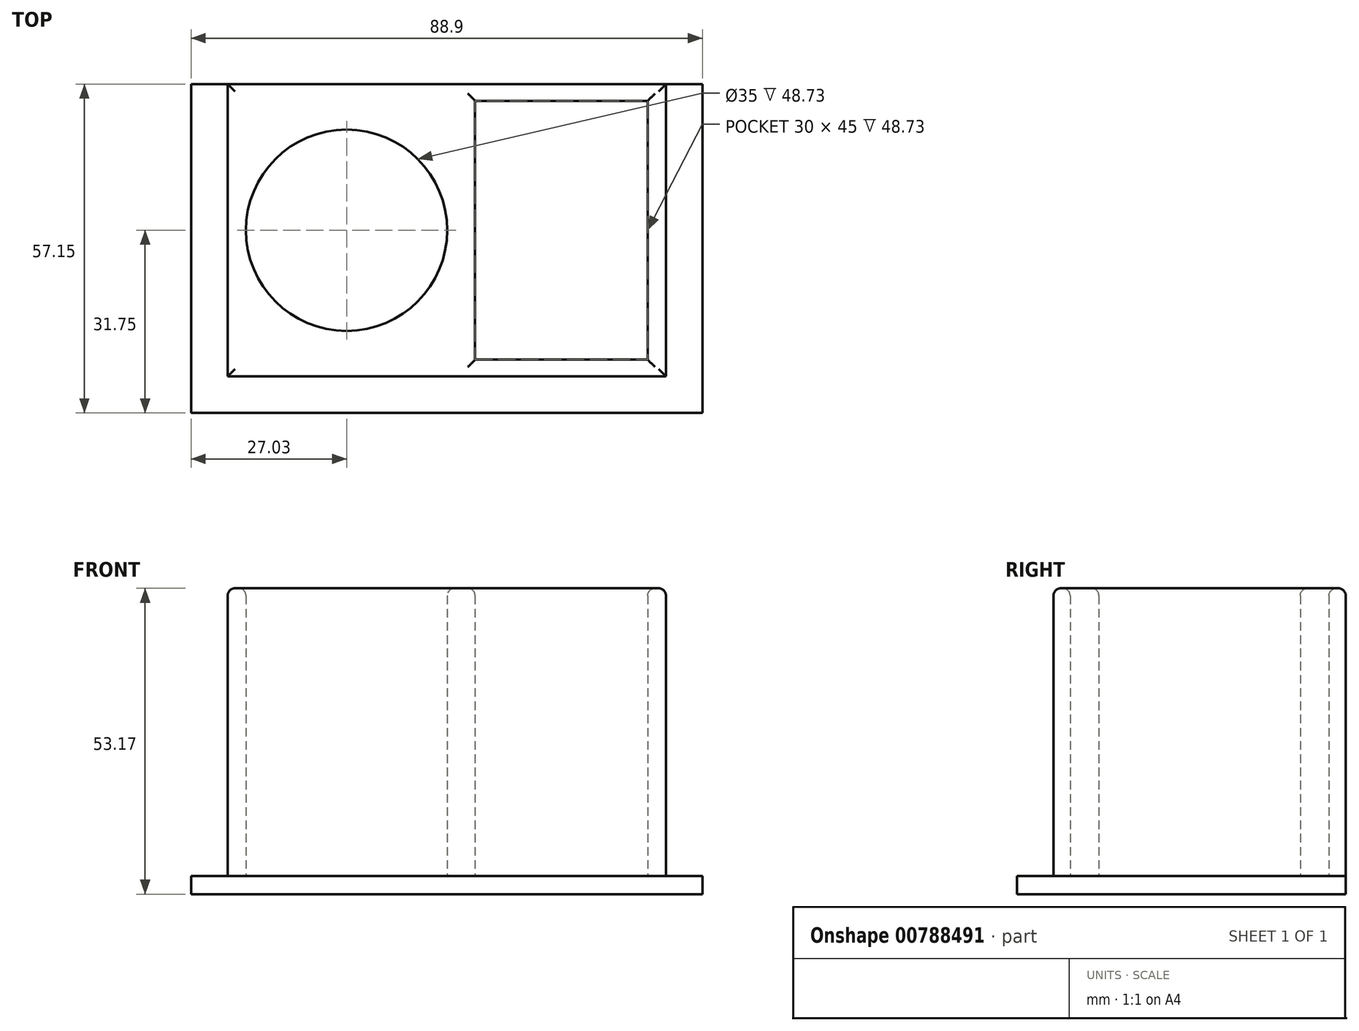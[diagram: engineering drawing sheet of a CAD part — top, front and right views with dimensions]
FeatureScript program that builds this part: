
annotation { "Feature Type Name" : "Feature", "Feature Type Description" : "" }
export const myFeature = defineFeature(function(context is Context, id is Id, definition is map)
    precondition{}
    {
        {
            var Q0;
            Q0=qCreatedBy(makeId("Top.planeOp"),FACE);
            var sketch = newSketch(context, id + "F0", { "sketchPlane" : qUnion([Q0])});
            skLineSegment(sketch, "E0.bottom", {"start": v(0, 0) * mm, "end": v(30, 0) * mm});
            skLineSegment(sketch, "E0.top", {"start": v(0, 45) * mm, "end": v(30, 45) * mm});
            skLineSegment(sketch, "E0.left", {"start": v(0, 0) * mm, "end": v(0, 45) * mm});
            skLineSegment(sketch, "E0.right", {"start": v(30, 0) * mm, "end": v(30, 45) * mm});
            skCircle(sketch, "E1", {"center": v(-22.35, 22.5) * mm, "radius": 17.5 * mm});
            skLineSegment(sketch, "E2.bottom", {"start": v(-43.03, 47.9) * mm, "end": v(33.17, 47.9) * mm});
            skLineSegment(sketch, "E2.top", {"start": v(-43.03, -2.9) * mm, "end": v(33.18, -2.9) * mm});
            skLineSegment(sketch, "E2.left", {"start": v(-43.03, 47.9) * mm, "end": v(-43.03, -2.9) * mm});
            skLineSegment(sketch, "E2.right", {"start": v(33.17, 47.9) * mm, "end": v(33.17, -2.9) * mm});
            skLineSegment(sketch, "E3", {"start": v(30, 22.5) * mm, "end": v(33.17, 22.5) * mm});
            skLineSegment(sketch, "E4", {"start": v(-43.03, 22.5) * mm, "end": v(-22.35, 22.5) * mm});
            skLineSegment(sketch, "E5", {"start": v(-43.03, 22.5) * mm, "end": v(-39.85, 22.5) * mm});
            skSolve(sketch);
        }
        {
            var Q0;
            {var subQ7=sQuery(id+"F0.wireOp",EDGE,"E0.bottom");Q0=makeQuery(id+"F0.imprint","IMPRINT",FACE,{"disambiguationData":[TD([[makeQuery(id+"F0.imprint","IMPRINT",EDGE,{"derivedFrom":subQ7}),-1.0]])]});}
            extrude(context, id + "F1", {"entities" : qUnion([Q0]), "depth" : 50 * mm, "offsetDistance" : 25.4 * mm});
        }
        {
            var Q0;
            Q0=makeQuery(id+"F1.opExtrude","CAP_FACE",FACE,{"disambiguationData":[OSD([sQuery(id+"F0.wireOp",EDGE,"E0.bottom"),sQuery(id+"F0.wireOp",EDGE,"E0.top"),sQuery(id+"F0.wireOp",EDGE,"E0.left"),sQuery(id+"F0.wireOp",EDGE,"E0.right"),sQuery(id+"F0.wireOp",EDGE,"E1"),sQuery(id+"F0.wireOp",EDGE,"E2.bottom"),sQuery(id+"F0.wireOp",EDGE,"E2.top"),sQuery(id+"F0.wireOp",EDGE,"E2.left"),sQuery(id+"F0.wireOp",EDGE,"E2.right")])],"isStart":true});
            var sketch = newSketch(context, id + "F2", { "sketchPlane" : qUnion([Q0])});
            skLineSegment(sketch, "E6.0", {"start": v(39.52, -54.25) * mm, "end": v(39.52, 9.25) * mm});
            skLineSegment(sketch, "E6.1", {"start": v(-49.38, -54.25) * mm, "end": v(39.52, -54.25) * mm});
            skLineSegment(sketch, "E6.2", {"start": v(-49.38, 9.25) * mm, "end": v(-49.38, -54.25) * mm});
            skLineSegment(sketch, "E6.3", {"start": v(39.52, 9.25) * mm, "end": v(-49.38, 9.25) * mm});
            skSolve(sketch);
        }
        {
            var Q0;
            Q0=makeQuery(id+"F2.imprint","IMPRINT",FACE,{"disambiguationData":[TD([[makeQuery(id+"F2.imprint","IMPRINT",EDGE,{"derivedFrom":makeQuery(id+"F1.opExtrude","CAP_EDGE",EDGE,{"disambiguationData":[OSD([sQuery(id+"F0.wireOp",EDGE,"E0.bottom")])],"isStart":true})}),1.0]])]});
            var Q1;
            Q1=makeQuery(id+"F2.imprint","IMPRINT",FACE,{"disambiguationData":[TD([[makeQuery(id+"F2.imprint","IMPRINT",EDGE,{"derivedFrom":sQuery(id+"F2.wireOp",EDGE,"E6.0")}),1.0]])]});
            var Q2;
            Q2=makeQuery(id+"F2.imprint","IMPRINT",FACE,{"disambiguationData":[TD([[makeQuery(id+"F2.imprint","IMPRINT",EDGE,{"derivedFrom":makeQuery(id+"F1.opExtrude","CAP_EDGE",EDGE,{"disambiguationData":[OSD([sQuery(id+"F0.wireOp",EDGE,"E0.bottom")])],"isStart":true})}),-1.0]])]});
            var Q3;
            Q3=makeQuery(id+"F2.imprint","IMPRINT",FACE,{"disambiguationData":[TD([[makeQuery(id+"F2.imprint","IMPRINT",EDGE,{"derivedFrom":makeQuery(id+"F1.opExtrude","CAP_EDGE",EDGE,{"disambiguationData":[OSD([sQuery(id+"F0.wireOp",EDGE,"E1")])],"isStart":true})}),-1.0]])]});
            extrude(context, id + "F3", {"entities" : qUnion([Q0, Q1, Q2, Q3]), "operationType" : NewBodyOperationType.ADD, "depth" : 3.17 * mm, "offsetDistance" : 25.4 * mm});
        }
        {
            var Q0;
            Q0=makeQuery(id+"F1.opExtrude","SWEPT_FACE",FACE,{"disambiguationData":[OSD([sQuery(id+"F0.wireOp",EDGE,"E2.bottom")])]});
            var sketch = newSketch(context, id + "F4", { "sketchPlane" : qUnion([Q0])});
            skLineSegment(sketch, "E7.bottom", {"start": v(-195.96, 150.21) * mm, "end": v(246.87, 150.21) * mm});
            skLineSegment(sketch, "E7.top", {"start": v(-195.96, -106.64) * mm, "end": v(246.87, -106.64) * mm});
            skLineSegment(sketch, "E7.left", {"start": v(-195.96, 150.21) * mm, "end": v(-195.96, -106.64) * mm});
            skLineSegment(sketch, "E7.right", {"start": v(246.87, 150.21) * mm, "end": v(246.87, -106.64) * mm});
            skSolve(sketch);
        }
        {
            var Q0;
            Q0 = qSketchRegion(id + "F4", true);
            extrude(context, id + "F5", {"entities" : qUnion([Q0]), "operationType" : NewBodyOperationType.REMOVE, "depth" : 25.4 * mm, "offsetDistance" : 25.4 * mm});
        }
        {
            var Q0;
            Q0=makeQuery(id+"F1.opExtrude","CAP_EDGE",EDGE,{"disambiguationData":[OSD([sQuery(id+"F0.wireOp",EDGE,"E0.left")])],"isStart":false});
            var Q1;
            Q1=makeQuery(id+"F1.opExtrude","CAP_FACE",FACE,{"disambiguationData":[OSD([sQuery(id+"F0.wireOp",EDGE,"E0.bottom"),sQuery(id+"F0.wireOp",EDGE,"E0.top"),sQuery(id+"F0.wireOp",EDGE,"E0.left"),sQuery(id+"F0.wireOp",EDGE,"E0.right"),sQuery(id+"F0.wireOp",EDGE,"E1"),sQuery(id+"F0.wireOp",EDGE,"E2.bottom"),sQuery(id+"F0.wireOp",EDGE,"E2.top"),sQuery(id+"F0.wireOp",EDGE,"E2.left"),sQuery(id+"F0.wireOp",EDGE,"E2.right")])],"isStart":false});
            var Q2;
            Q2=makeQuery(id+"F1.opExtrude","CAP_EDGE",EDGE,{"disambiguationData":[OSD([sQuery(id+"F0.wireOp",EDGE,"E0.right")])],"isStart":false});
            var Q3;
            Q3=makeQuery(id+"F1.opExtrude","CAP_EDGE",EDGE,{"disambiguationData":[OSD([sQuery(id+"F0.wireOp",EDGE,"E0.top")])],"isStart":false});
            var Q4;
            Q4=makeQuery(id+"F1.opExtrude","CAP_EDGE",EDGE,{"disambiguationData":[OSD([sQuery(id+"F0.wireOp",EDGE,"E1")])],"isStart":false});
            var Q5;
            Q5=makeQuery(id+"F1.opExtrude","CAP_EDGE",EDGE,{"disambiguationData":[OSD([sQuery(id+"F0.wireOp",EDGE,"E2.bottom")])],"isStart":false});
            fillet(context, id + "F6", {"entities" : qUnion([Q0, Q1, Q2, Q3, Q4, Q5]), "radius" : 1.27 * mm, "tangentPropagation" : true, "allowEdgeOverflow" : false});
        }
    });
